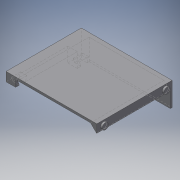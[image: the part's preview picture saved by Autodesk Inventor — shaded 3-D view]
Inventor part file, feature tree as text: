
AUTODESK INVENTOR PART (.ipt)
format: ipt  version: 2016 SP2 (Build 200236200, 236)  size: 135,680 bytes
history: native  units: mm
features: sketch x5, other x3
ambient origin geometry x8: Origin, YZ Plane, XZ Plane, XY Plane, X Axis, Y Axis, Z Axis, Center Point
bodies: Volumenkörper1 (feature_tree)
feature tree (8):
  other  "Batcap3.ipt"
  other  "Volumenkörper1::Batcap3.ipt"
  other  "Bezeichnung1"
  sketch  "Skizze1"  dims[d0=10.0mm]
  sketch  "Skizze2"
  sketch  "Skizze3"
  sketch  "Skizze4"
  sketch  "Skizze5"
